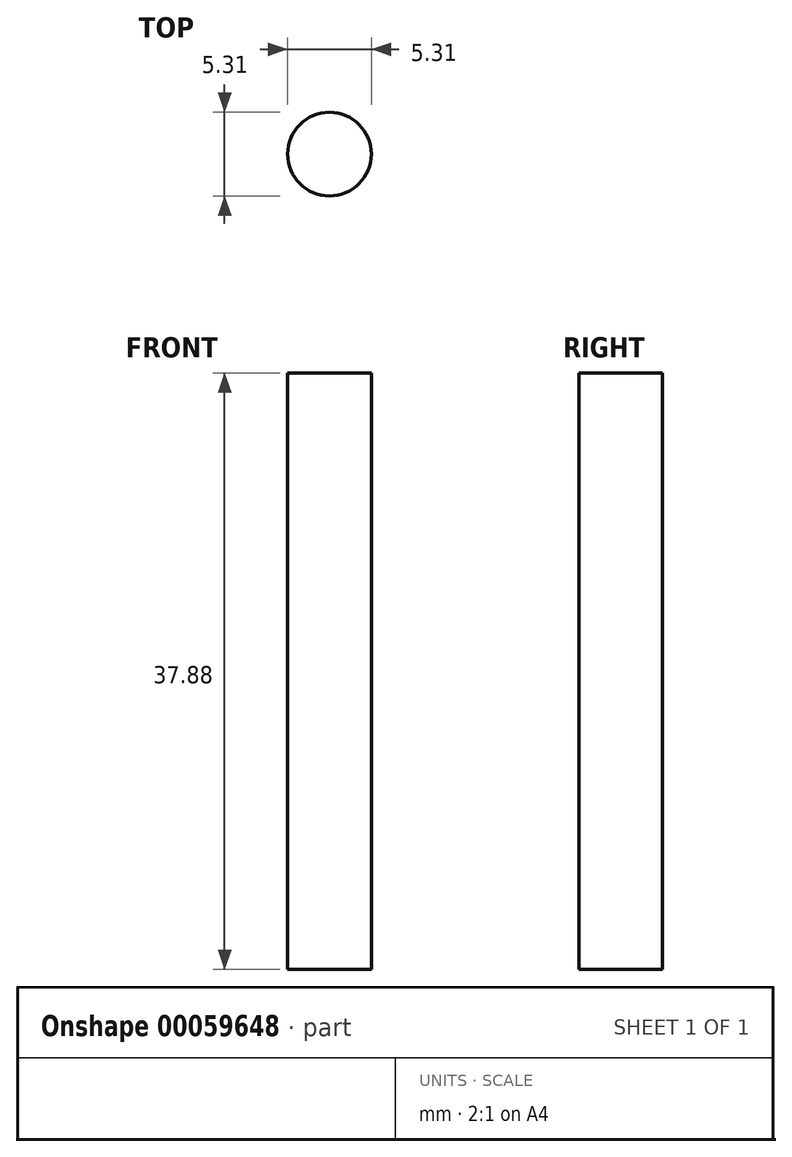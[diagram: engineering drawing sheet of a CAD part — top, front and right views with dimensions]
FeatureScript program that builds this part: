
annotation { "Feature Type Name" : "Feature", "Feature Type Description" : "" }
export const myFeature = defineFeature(function(context is Context, id is Id, definition is map)
    precondition{}
    {
        {
            var Q0;
            Q0=qCreatedBy(makeId("Top.planeOp"),FACE);
            var sketch = newSketch(context, id + "F0", { "sketchPlane" : qUnion([Q0])});
            skCircle(sketch, "E0", {"center": v(-45.41, 23.35) * mm, "radius": 2.66 * mm});
            skSolve(sketch);
        }
        {
            var Q0;
            Q0 = qSketchRegion(id + "F0", true);
            extrude(context, id + "F1", {"entities" : qUnion([Q0]), "depth" : 37.88 * mm});
        }
    });
